# Revit family: bm-00012_abr782r
name_source: partatom
category: Plumbing Fixtures
revit_build: Autodesk Revit LT 2016 (Build: 20150220_1215(x64)
units: mm (PartAtom-declared; Revit-internal decimal feet)

## family parameters
Cut with Voids When Loaded = No
Host = Face
OmniClass Number = 23.45.05.14.21
OmniClass Title = Bathtubs
Part Type = Normal
Room Calculation Point = No
Round Connector Dimension = Use Radius
Shared = No

## types (1)
- ABR782R
    04 CSI = 22 41 19
    95 CSI = 15410
    Assembly Code = D2010510
    Blower Motor Horsepower (HP) = 1
    Bottom Plate = Metal - TOTO - LifeKoat - Brass - Polished
    CAD Drawing URL = http://assets.totousa.com
    CW Connection = No
    CWFU = 0
    Color Availability = #01  Cotton, #12  Sedona Beige
    Default Elevation = 0"
    Depth = 60"
    Description = Tile-In Air Bath
    Finish = Metal - TOTO - Chrome - Polished
    Frequency = 60 Hz
    Full Load Amps = 10 A
    HW Connection = No
    HWFU = 0
    Height = 2 7/8"
    Industry Standards = 1200 VA
    Installation URL = http://assets.totousa.com
    Manufacturer = TOTO USA, Inc.
    Manufacturer Fax = (770) 282-0002
    Model = ABA782R
    Number of Poles = 1
    Parts Manual URL = http://assets.totousa.com
    Series = Clayton
    Shipping Weight = 116.00 lb
    Spec Sheet URL = http://assets.totousa.com
    Style = Traditional
    Subcategory = Bathtubs
    Toto BIM Number = BM-00012
    URL = http://www.totousa.com
    Vent Connection = Yes
    Voltage = 120 V
    WFU = 0
    Warranty = 1 Year Limited Warranty on acrylic tub; 1 Year Limited Warranty on components and parts
    Warranty URL = http://www.totousa.com
    Waste Connection = Yes
    Waste Connection NPT = 2"
    Waste Connection Radius = 1"
    Width = 32"

## geometry (parser evidence)
native form markers: Blend x16, Sweep x4
no freeform markers — native parametric forms only
